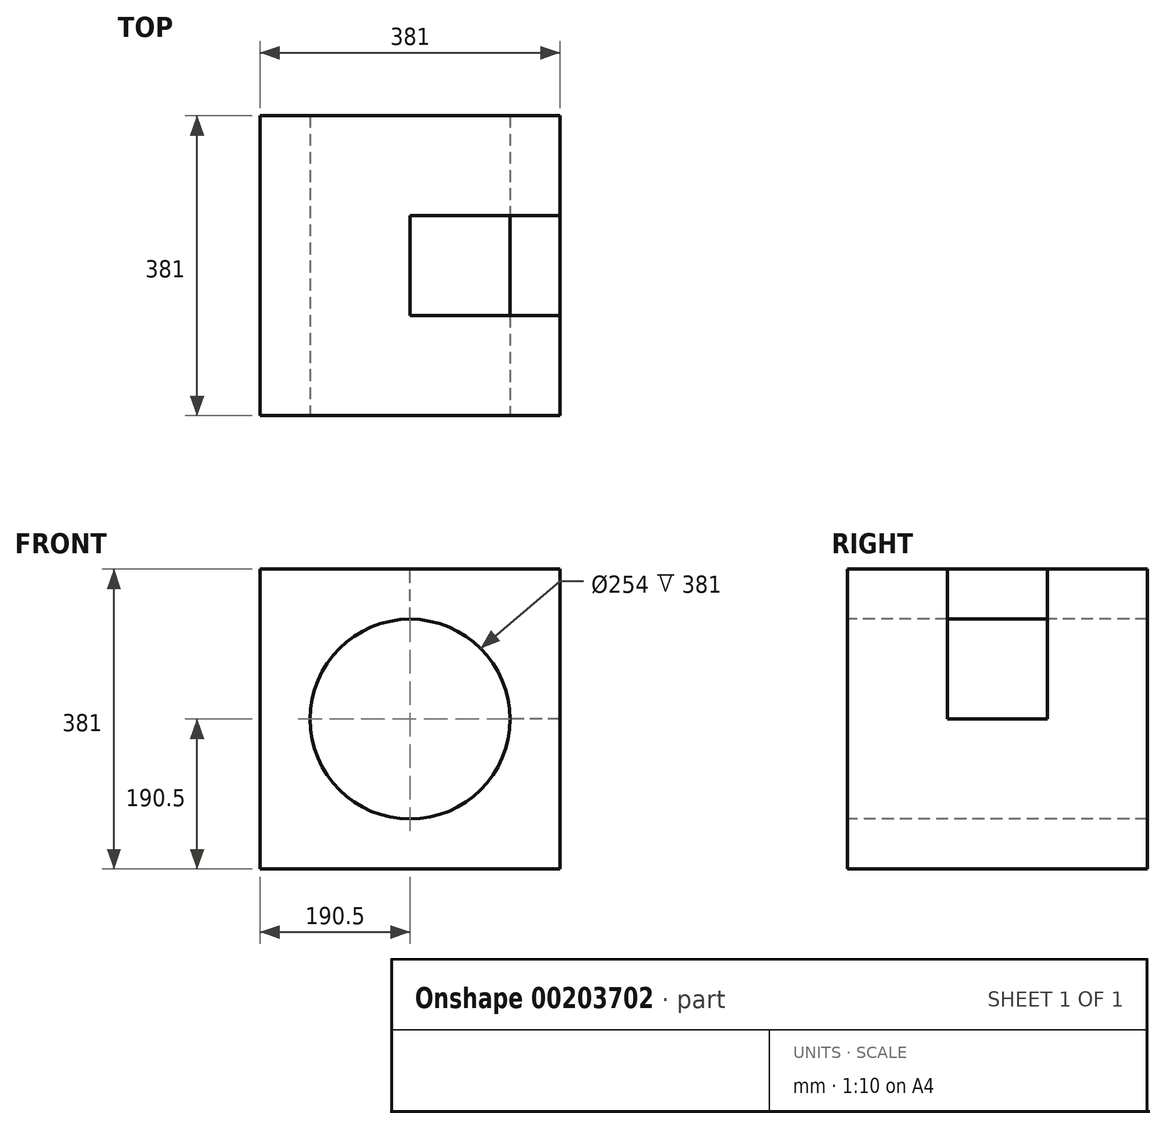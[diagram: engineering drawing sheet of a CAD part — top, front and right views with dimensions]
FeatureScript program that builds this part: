
annotation { "Feature Type Name" : "Feature", "Feature Type Description" : "" }
export const myFeature = defineFeature(function(context is Context, id is Id, definition is map)
    precondition{}
    {
        {
            var Q0;
            Q0=qCreatedBy(makeId("Front.planeOp"),FACE);
            var sketch = newSketch(context, id + "F0", { "sketchPlane" : qUnion([Q0])});
            skLineSegment(sketch, "E0.bottom", {"start": v(-190.5, 190.5) * mm, "end": v(190.5, 190.5) * mm});
            skLineSegment(sketch, "E0.top", {"start": v(-190.5, -190.5) * mm, "end": v(190.5, -190.5) * mm});
            skLineSegment(sketch, "E0.left", {"start": v(-190.5, 190.5) * mm, "end": v(-190.5, -190.5) * mm});
            skLineSegment(sketch, "E0.right", {"start": v(190.5, 190.5) * mm, "end": v(190.5, -190.5) * mm});
            skPoint(sketch, "E0.middle", {"position": v(0, 0) * mm});
            skSolve(sketch);
        }
        {
            var Q0;
            Q0=makeQuery(id+"F0.imprint","IMPRINT",FACE,{"disambiguationData":[TD([[makeQuery(id+"F0.imprint","IMPRINT",EDGE,{"derivedFrom":sQuery(id+"F0.wireOp",EDGE,"E0.bottom")}),-1.0]])]});
            var sketch = newSketch(context, id + "F1", { "sketchPlane" : qUnion([Q0])});
            skCircle(sketch, "E1", {"center": v(0, 0) * mm, "radius": 127 * mm});
            skSolve(sketch);
        }
        {
            var Q0;
            Q0=makeQuery(id+"F1.imprint","IMPRINT",FACE,{"disambiguationData":[TD([[makeQuery(id+"F1.imprint","IMPRINT",EDGE,{"derivedFrom":sQuery(id+"F1.wireOp",EDGE,"E1")}),-1.0]])]});
            extrude(context, id + "F2", {"entities" : qUnion([Q0]), "oppositeDirection" : true, "depth" : 381 * mm});
        }
        {
            var Q0;
            Q0=makeQuery(id+"F2.opExtrude","SWEPT_FACE",FACE,{"disambiguationData":[OSD([sQuery(id+"F0.wireOp",EDGE,"E0.bottom")])]});
            var sketch = newSketch(context, id + "F3", { "sketchPlane" : qUnion([Q0])});
            skLineSegment(sketch, "E2.bottom", {"start": v(190.5, 254) * mm, "end": v(0, 254) * mm});
            skLineSegment(sketch, "E2.top", {"start": v(190.5, 127) * mm, "end": v(0, 127) * mm});
            skLineSegment(sketch, "E2.left", {"start": v(190.5, 254) * mm, "end": v(190.5, 127) * mm});
            skLineSegment(sketch, "E2.right", {"start": v(0, 254) * mm, "end": v(0, 127) * mm});
            skSolve(sketch);
        }
        {
            var Q0;
            Q0=makeQuery(id+"F3.imprint","IMPRINT",FACE,{"disambiguationData":[TD([[makeQuery(id+"F3.imprint","IMPRINT",EDGE,{"derivedFrom":sQuery(id+"F3.wireOp",EDGE,"E2.bottom")}),1.0]])]});
            extrude(context, id + "F4", {"entities" : qUnion([Q0]), "operationType" : NewBodyOperationType.REMOVE, "oppositeDirection" : true, "depth" : 190.5 * mm});
        }
    });
